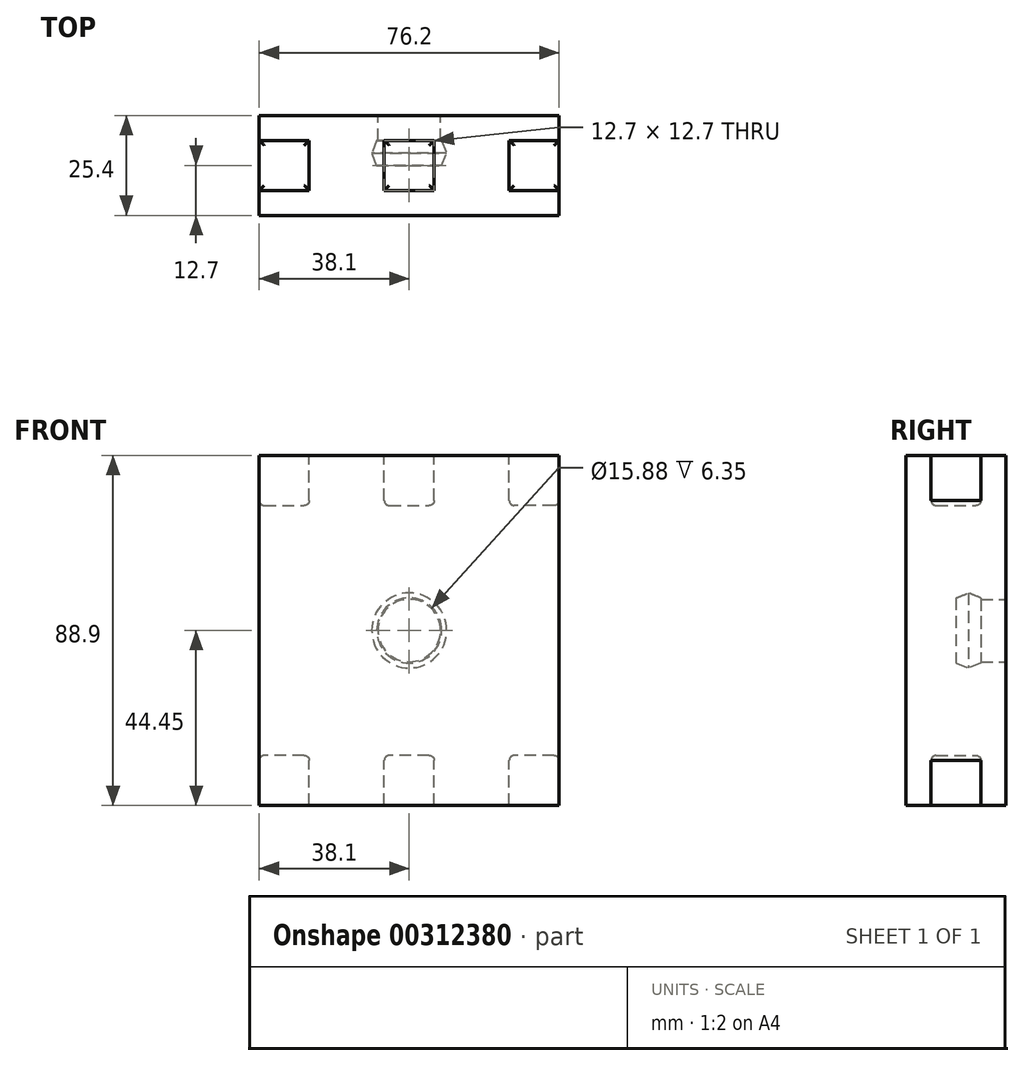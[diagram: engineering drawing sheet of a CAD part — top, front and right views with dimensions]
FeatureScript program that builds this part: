
annotation { "Feature Type Name" : "Feature", "Feature Type Description" : "" }
export const myFeature = defineFeature(function(context is Context, id is Id, definition is map)
    precondition{}
    {
        {
            var Q0;
            Q0=qCreatedBy(makeId("Front.planeOp"),FACE);
            var sketch = newSketch(context, id + "F0", { "sketchPlane" : qUnion([Q0])});
            skLineSegment(sketch, "E0.bottom", {"start": v(-38.1, -44.45) * mm, "end": v(38.1, -44.45) * mm});
            skLineSegment(sketch, "E0.top", {"start": v(-38.1, 44.45) * mm, "end": v(38.1, 44.45) * mm});
            skLineSegment(sketch, "E0.left", {"start": v(-38.1, -44.45) * mm, "end": v(-38.1, 44.45) * mm});
            skLineSegment(sketch, "E0.right", {"start": v(38.1, -44.45) * mm, "end": v(38.1, 44.45) * mm});
            skPoint(sketch, "E0.middle", {"position": v(0, 0) * mm});
            skSolve(sketch);
        }
        {
            var Q0;
            Q0=makeQuery(id+"F0.imprint","IMPRINT",FACE,{"disambiguationData":[TD([[makeQuery(id+"F0.imprint","IMPRINT",EDGE,{"derivedFrom":sQuery(id+"F0.wireOp",EDGE,"E0.bottom")}),1.0]])]});
            extrude(context, id + "F1", {"entities" : qUnion([Q0]), "endBound" : BoundingType.SYMMETRIC, "depth" : 25.4 * mm});
        }
        {
            var Q0;
            Q0=makeQuery(id+"F1.opExtrude","SWEPT_FACE",FACE,{"disambiguationData":[OSD([sQuery(id+"F0.wireOp",EDGE,"E0.top")])]});
            var sketch = newSketch(context, id + "F2", { "sketchPlane" : qUnion([Q0])});
            skLineSegment(sketch, "E1.bottom", {"start": v(-6.35, -6.35) * mm, "end": v(6.35, -6.35) * mm});
            skLineSegment(sketch, "E1.top", {"start": v(-6.35, 6.35) * mm, "end": v(6.35, 6.35) * mm});
            skLineSegment(sketch, "E1.left", {"start": v(-6.35, -6.35) * mm, "end": v(-6.35, 6.35) * mm});
            skLineSegment(sketch, "E1.right", {"start": v(6.35, -6.35) * mm, "end": v(6.35, 6.35) * mm});
            skPoint(sketch, "E1.middle", {"position": v(0, 0) * mm});
            skLineSegment(sketch, "E2.bottom", {"start": v(38.1, -6.35) * mm, "end": v(25.4, -6.35) * mm});
            skLineSegment(sketch, "E2.top", {"start": v(38.1, 6.35) * mm, "end": v(25.4, 6.35) * mm});
            skLineSegment(sketch, "E2.left", {"start": v(38.1, -6.35) * mm, "end": v(38.1, 6.35) * mm});
            skLineSegment(sketch, "E2.right", {"start": v(25.4, -6.35) * mm, "end": v(25.4, 6.35) * mm});
            skPoint(sketch, "E2.middle", {"position": v(31.75, 0) * mm});
            skLineSegment(sketch, "E3.bottom", {"start": v(-38.1, -6.35) * mm, "end": v(-25.4, -6.35) * mm});
            skLineSegment(sketch, "E3.top", {"start": v(-38.1, 6.35) * mm, "end": v(-25.4, 6.35) * mm});
            skLineSegment(sketch, "E3.left", {"start": v(-38.1, -6.35) * mm, "end": v(-38.1, 6.35) * mm});
            skLineSegment(sketch, "E3.right", {"start": v(-25.4, -6.35) * mm, "end": v(-25.4, 6.35) * mm});
            skPoint(sketch, "E3.middle", {"position": v(-31.75, 0) * mm});
            skSolve(sketch);
        }
        {
            var Q0;
            {var subQ0=sQuery(id+"F0.wireOp",EDGE,"E0.bottom");Q0=makeQuery(id+"F4.boolean.opBoolean","MERGE",FACE,{"derivedFrom":[makeQuery(id+"F1.opExtrude","SWEPT_FACE",FACE,{"disambiguationData":[OSD([subQ0])]}),makeQuery(id+"F4.opExtrude","SWEPT_FACE",FACE,{"disambiguationData":[OSD([subQ0,sQuery(id+"F0.wireOp",EDGE,"E0.left")])]}),makeQuery(id+"F4.opExtrude","SWEPT_FACE",FACE,{"disambiguationData":[OSD([subQ0,sQuery(id+"F0.wireOp",EDGE,"E0.right")])]})]});}
            var sketch = newSketch(context, id + "F3", { "sketchPlane" : qUnion([Q0])});
            skLineSegment(sketch, "E4.bottom", {"start": v(6.35, 6.35) * mm, "end": v(-6.35, 6.35) * mm});
            skLineSegment(sketch, "E4.top", {"start": v(6.35, -6.35) * mm, "end": v(-6.35, -6.35) * mm});
            skLineSegment(sketch, "E4.left", {"start": v(6.35, 6.35) * mm, "end": v(6.35, -6.35) * mm});
            skLineSegment(sketch, "E4.right", {"start": v(-6.35, 6.35) * mm, "end": v(-6.35, -6.35) * mm});
            skPoint(sketch, "E4.middle", {"position": v(0, 0) * mm});
            skLineSegment(sketch, "E5.bottom", {"start": v(38.1, -6.35) * mm, "end": v(25.4, -6.35) * mm});
            skLineSegment(sketch, "E5.top", {"start": v(38.1, 6.35) * mm, "end": v(25.4, 6.35) * mm});
            skLineSegment(sketch, "E5.left", {"start": v(38.1, -6.35) * mm, "end": v(38.1, 6.35) * mm});
            skLineSegment(sketch, "E5.right", {"start": v(25.4, -6.35) * mm, "end": v(25.4, 6.35) * mm});
            skPoint(sketch, "E5.middle", {"position": v(31.75, 0) * mm});
            skLineSegment(sketch, "E6.bottom", {"start": v(-25.4, -6.35) * mm, "end": v(-38.1, -6.35) * mm});
            skLineSegment(sketch, "E6.top", {"start": v(-25.4, 6.35) * mm, "end": v(-38.1, 6.35) * mm});
            skLineSegment(sketch, "E6.left", {"start": v(-25.4, -6.35) * mm, "end": v(-25.4, 6.35) * mm});
            skLineSegment(sketch, "E6.right", {"start": v(-38.1, -6.35) * mm, "end": v(-38.1, 6.35) * mm});
            skPoint(sketch, "E6.middle", {"position": v(-31.75, 0) * mm});
            skSolve(sketch);
        }
        {
            var Q0;
            Q0=makeQuery(id+"F1.opExtrude","SWEPT_FACE",FACE,{"disambiguationData":[OSD([sQuery(id+"F0.wireOp",EDGE,"E0.left")])]});
            var Q1;
            Q1=makeQuery(id+"F1.opExtrude","SWEPT_FACE",FACE,{"disambiguationData":[OSD([sQuery(id+"F0.wireOp",EDGE,"E0.right")])]});
            extrude(context, id + "F4", {"entities" : qUnion([Q0, Q1]), "operationType" : NewBodyOperationType.ADD, "endBound" : BoundingType.SYMMETRIC, "depth" : 25.4 * mm});
        }
        {
            var Q0;
            Q0=makeQuery(id+"F2.imprint","IMPRINT",FACE,{"disambiguationData":[TD([[makeQuery(id+"F2.imprint","IMPRINT",EDGE,{"derivedFrom":sQuery(id+"F2.wireOp",EDGE,"E3.bottom")}),1.0]])]});
            var Q1;
            Q1=makeQuery(id+"F2.imprint","IMPRINT",FACE,{"disambiguationData":[TD([[makeQuery(id+"F2.imprint","IMPRINT",EDGE,{"derivedFrom":sQuery(id+"F2.wireOp",EDGE,"E1.bottom")}),1.0]])]});
            var Q2;
            Q2=makeQuery(id+"F2.imprint","IMPRINT",FACE,{"disambiguationData":[TD([[makeQuery(id+"F2.imprint","IMPRINT",EDGE,{"derivedFrom":sQuery(id+"F2.wireOp",EDGE,"E2.bottom")}),-1.0]])]});
            var Q3;
            Q3=makeQuery(id+"F3.imprint","IMPRINT",FACE,{"disambiguationData":[TD([[makeQuery(id+"F3.imprint","IMPRINT",EDGE,{"derivedFrom":sQuery(id+"F3.wireOp",EDGE,"E6.bottom")}),-1.0]])]});
            var Q4;
            Q4=makeQuery(id+"F3.imprint","IMPRINT",FACE,{"disambiguationData":[TD([[makeQuery(id+"F3.imprint","IMPRINT",EDGE,{"derivedFrom":sQuery(id+"F3.wireOp",EDGE,"E4.bottom")}),1.0]])]});
            var Q5;
            Q5=makeQuery(id+"F3.imprint","IMPRINT",FACE,{"disambiguationData":[TD([[makeQuery(id+"F3.imprint","IMPRINT",EDGE,{"derivedFrom":sQuery(id+"F3.wireOp",EDGE,"E5.bottom")}),-1.0]])]});
            extrude(context, id + "F5", {"entities" : qUnion([Q0, Q1, Q2, Q3, Q4, Q5]), "operationType" : NewBodyOperationType.REMOVE, "endBound" : BoundingType.SYMMETRIC, "oppositeDirection" : true, "depth" : 25.4 * mm});
        }
        {
            var Q0;
            Q0=makeQuery(id+"F5.boolean.opBoolean","COPY",FACE,{"derivedFrom":makeQuery(id+"F5.opExtrude","CAP_FACE",FACE,{"disambiguationData":[OSD([sQuery(id+"F2.wireOp",EDGE,"E3.bottom"),sQuery(id+"F2.wireOp",EDGE,"E3.top"),sQuery(id+"F2.wireOp",EDGE,"E3.left"),sQuery(id+"F2.wireOp",EDGE,"E3.right")])],"isStart":false})});
            var Q1;
            Q1=makeQuery(id+"F5.boolean.opBoolean","COPY",FACE,{"derivedFrom":makeQuery(id+"F5.opExtrude","CAP_FACE",FACE,{"disambiguationData":[OSD([sQuery(id+"F2.wireOp",EDGE,"E1.bottom"),sQuery(id+"F2.wireOp",EDGE,"E1.top"),sQuery(id+"F2.wireOp",EDGE,"E1.left"),sQuery(id+"F2.wireOp",EDGE,"E1.right")])],"isStart":false})});
            var Q2;
            Q2=makeQuery(id+"F5.boolean.opBoolean","COPY",FACE,{"derivedFrom":makeQuery(id+"F5.opExtrude","CAP_FACE",FACE,{"disambiguationData":[OSD([sQuery(id+"F2.wireOp",EDGE,"E2.bottom"),sQuery(id+"F2.wireOp",EDGE,"E2.top"),sQuery(id+"F2.wireOp",EDGE,"E2.left"),sQuery(id+"F2.wireOp",EDGE,"E2.right")])],"isStart":false})});
            var Q3;
            Q3=makeQuery(id+"F5.boolean.opBoolean","COPY",EDGE,{"derivedFrom":makeQuery(id+"F5.opExtrude","CAP_EDGE",EDGE,{"disambiguationData":[OSD([sQuery(id+"F2.wireOp",EDGE,"E2.left")])],"isStart":false})});
            var Q4;
            Q4=makeQuery(id+"F5.boolean.opBoolean","COPY",FACE,{"derivedFrom":makeQuery(id+"F5.opExtrude","CAP_FACE",FACE,{"disambiguationData":[OSD([sQuery(id+"F3.wireOp",EDGE,"E6.bottom"),sQuery(id+"F3.wireOp",EDGE,"E6.top"),sQuery(id+"F3.wireOp",EDGE,"E6.left"),sQuery(id+"F3.wireOp",EDGE,"E6.right")])],"isStart":true})});
            var Q5;
            Q5=makeQuery(id+"F5.boolean.opBoolean","COPY",FACE,{"derivedFrom":makeQuery(id+"F5.opExtrude","CAP_FACE",FACE,{"disambiguationData":[OSD([sQuery(id+"F3.wireOp",EDGE,"E4.bottom"),sQuery(id+"F3.wireOp",EDGE,"E4.top"),sQuery(id+"F3.wireOp",EDGE,"E4.left"),sQuery(id+"F3.wireOp",EDGE,"E4.right")])],"isStart":true})});
            var Q6;
            Q6=makeQuery(id+"F5.boolean.opBoolean","COPY",FACE,{"derivedFrom":makeQuery(id+"F5.opExtrude","CAP_FACE",FACE,{"disambiguationData":[OSD([sQuery(id+"F3.wireOp",EDGE,"E5.bottom"),sQuery(id+"F3.wireOp",EDGE,"E5.top"),sQuery(id+"F3.wireOp",EDGE,"E5.left"),sQuery(id+"F3.wireOp",EDGE,"E5.right")])],"isStart":true})});
            fillet(context, id + "F6", {"entities" : qUnion([Q0, Q1, Q2, Q3, Q4, Q5, Q6]), "radius" : 1.27 * mm, "tangentPropagation" : true, "allowEdgeOverflow" : false});
        }
        {
            var Q0;
            Q0=makeQuery(id+"F4.opExtrude","CAP_FACE",FACE,{"disambiguationData":[OSD([sQuery(id+"F0.wireOp",EDGE,"E0.right")])],"isStart":true});
            var Q1;
            Q1=makeQuery(id+"F4.opExtrude","CAP_FACE",FACE,{"disambiguationData":[OSD([sQuery(id+"F0.wireOp",EDGE,"E0.left")])],"isStart":false});
            extrude(context, id + "F7", {"entities" : qUnion([Q0, Q1]), "operationType" : NewBodyOperationType.REMOVE, "endBound" : BoundingType.SYMMETRIC, "oppositeDirection" : true, "depth" : 25.4 * mm});
        }
        {
            var Q0;
            {var subQ0=sQuery(id+"F0.wireOp",EDGE,"E0.right");var subQ1=sQuery(id+"F0.wireOp",EDGE,"E0.left");Q0=makeQuery(id+"F4.boolean.opBoolean","MERGE",FACE,{"derivedFrom":[makeQuery(id+"F1.opExtrude","CAP_FACE",FACE,{"disambiguationData":[OSD([sQuery(id+"F0.wireOp",EDGE,"E0.bottom"),sQuery(id+"F0.wireOp",EDGE,"E0.top"),subQ1,subQ0])],"isStart":true}),makeQuery(id+"F4.opExtrude","SWEPT_FACE",FACE,{"disambiguationData":[OSD([subQ1]),TDD([makeQuery(id+"F1.opExtrude","CAP_EDGE",EDGE,{"disambiguationData":[OSD([subQ1])],"isStart":true})])]}),makeQuery(id+"F4.opExtrude","SWEPT_FACE",FACE,{"disambiguationData":[OSD([subQ0]),TDD([makeQuery(id+"F1.opExtrude","CAP_EDGE",EDGE,{"disambiguationData":[OSD([subQ0])],"isStart":true})])]})]});}
            var sketch = newSketch(context, id + "F8", { "sketchPlane" : qUnion([Q0])});
            skCircle(sketch, "E7", {"center": v(0, 0) * mm, "radius": 7.94 * mm});
            skSolve(sketch);
        }
        {
            var Q0;
            Q0=makeQuery(id+"F8.imprint","IMPRINT",FACE,{"disambiguationData":[TD([[makeQuery(id+"F8.imprint","IMPRINT",EDGE,{"derivedFrom":sQuery(id+"F8.wireOp",EDGE,"E7")}),1.0]])]});
            extrude(context, id + "F9", {"entities" : qUnion([Q0]), "operationType" : NewBodyOperationType.REMOVE, "oppositeDirection" : true, "depth" : 12.7 * mm});
        }
        {
            var Q0;
            Q0=makeQuery(id+"F9.boolean.opBoolean","COPY",FACE,{"derivedFrom":makeQuery(id+"F9.opExtrude","CAP_FACE",FACE,{"disambiguationData":[OSD([sQuery(id+"F8.wireOp",EDGE,"E7")])],"isStart":false})});
            var sketch = newSketch(context, id + "F10", { "sketchPlane" : qUnion([Q0])});
            skCircle(sketch, "E8", {"center": v(0, 0) * mm, "radius": 9.53 * mm});
            skSolve(sketch);
        }
        {
            var Q0;
            Q0 = qSketchRegion(id + "F10", true);
            extrude(context, id + "F11", {"entities" : qUnion([Q0]), "operationType" : NewBodyOperationType.REMOVE, "depth" : 6.35 * mm});
        }
        {
            var Q0;
            Q0=makeQuery(id+"F11.boolean.opBoolean","COPY",EDGE,{"derivedFrom":makeQuery(id+"F11.opExtrude","CAP_EDGE",EDGE,{"disambiguationData":[OSD([sQuery(id+"F10.wireOp",EDGE,"E8")])],"isStart":true})});
            var Q1;
            Q1=makeQuery(id+"F11.boolean.opBoolean","COPY",EDGE,{"derivedFrom":makeQuery(id+"F11.opExtrude","CAP_EDGE",EDGE,{"disambiguationData":[OSD([sQuery(id+"F10.wireOp",EDGE,"E8")])],"isStart":false})});
            chamfer(context, id + "F12", {"entities" : qUnion([Q0, Q1]), "chamferType" : ChamferType.TWO_OFFSETS, "width1" : 3.17 * mm, "oppositeDirection" : true, "width2" : 1.27 * mm, "tangentPropagation" : true});
        }
    });
